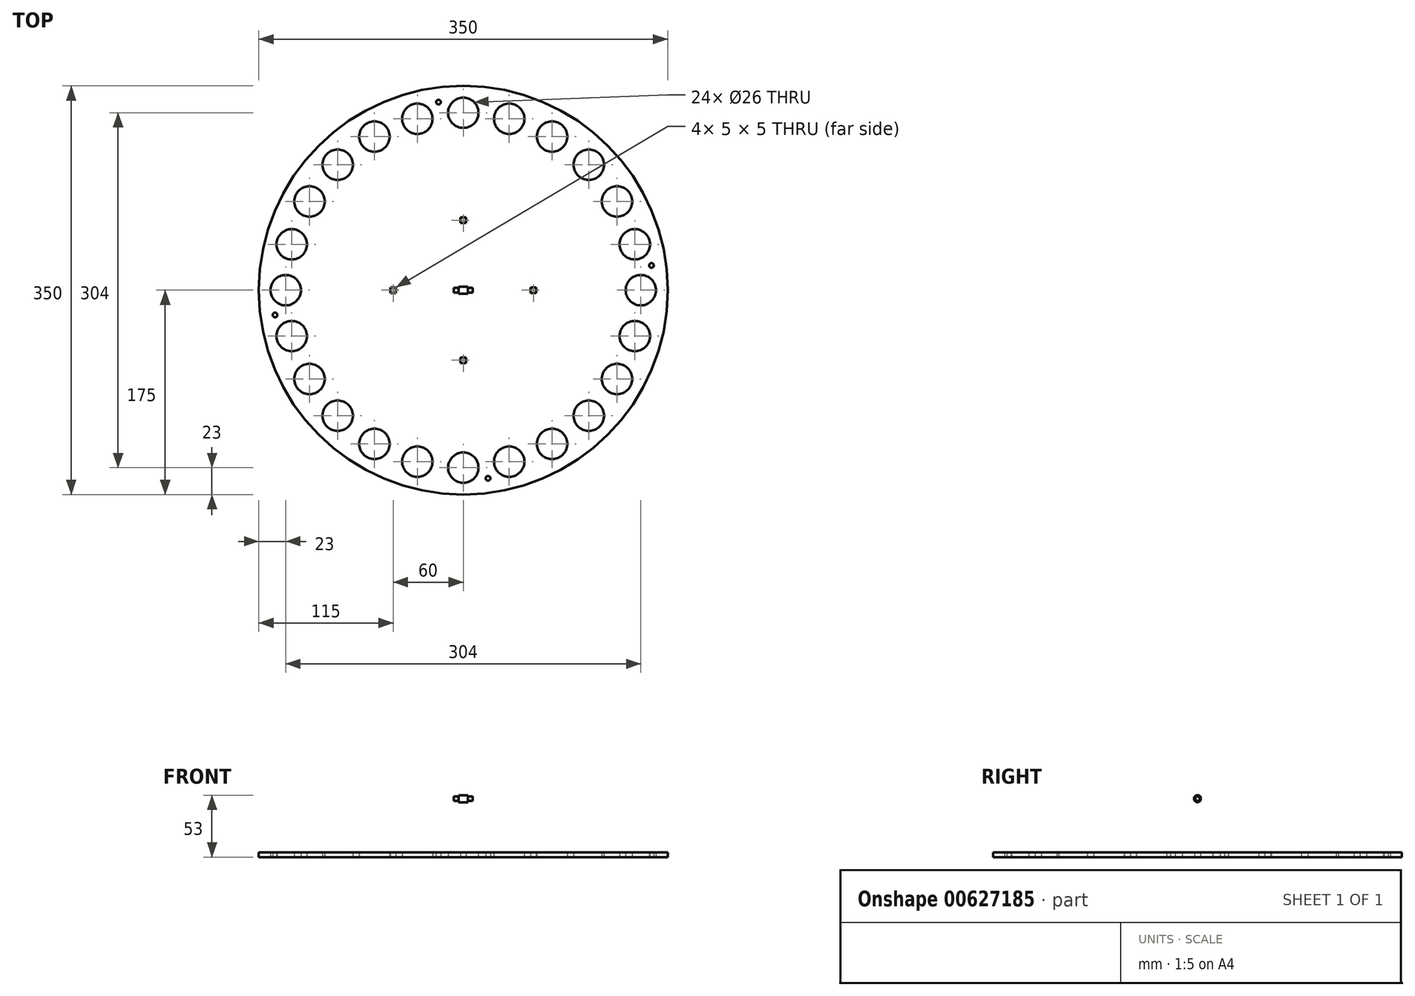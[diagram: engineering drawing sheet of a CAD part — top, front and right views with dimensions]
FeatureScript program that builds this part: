
annotation { "Feature Type Name" : "Feature", "Feature Type Description" : "" }
export const myFeature = defineFeature(function(context is Context, id is Id, definition is map)
    precondition{}
    {
        {
            var Q0;
            Q0=qCreatedBy(makeId("Top.planeOp"),FACE);
            var sketch = newSketch(context, id + "F0", { "sketchPlane" : qUnion([Q0])});
            skCircle(sketch, "E0", {"center": v(0, 0) * mm, "radius": 175 * mm});
            skLineSegment(sketch, "E1", {"start": v(0, 210.07) * mm, "end": v(0, -239.93) * mm, "construction": true});
            skLineSegment(sketch, "E2", {"start": v(-226.4, 0) * mm, "end": v(223.6, 0) * mm, "construction": true});
            skCircle(sketch, "E3", {"center": v(0, 152) * mm, "radius": 13 * mm});
            skCircle(sketch, "E4.1.1", {"center": v(-39.34, 146.82) * mm, "radius": 13 * mm});
            skCircle(sketch, "E4.2.1", {"center": v(-76, 131.64) * mm, "radius": 13 * mm});
            skCircle(sketch, "E4.3.1", {"center": v(-107.48, 107.48) * mm, "radius": 13 * mm});
            skCircle(sketch, "E4.4.1", {"center": v(-131.64, 76) * mm, "radius": 13 * mm});
            skCircle(sketch, "E4.5.1", {"center": v(-146.82, 39.34) * mm, "radius": 13 * mm});
            skCircle(sketch, "E4.6.1", {"center": v(-152, 0) * mm, "radius": 13 * mm});
            skCircle(sketch, "E4.7.1", {"center": v(-146.82, -39.34) * mm, "radius": 13 * mm});
            skCircle(sketch, "E4.8.1", {"center": v(-131.64, -76) * mm, "radius": 13 * mm});
            skCircle(sketch, "E4.9.1", {"center": v(-107.48, -107.48) * mm, "radius": 13 * mm});
            skCircle(sketch, "E4.10.1", {"center": v(-76, -131.64) * mm, "radius": 13 * mm});
            skCircle(sketch, "E4.11.1", {"center": v(-39.34, -146.82) * mm, "radius": 13 * mm});
            skCircle(sketch, "E4.12.1", {"center": v(0, -152) * mm, "radius": 13 * mm});
            skCircle(sketch, "E4.13.1", {"center": v(39.34, -146.82) * mm, "radius": 13 * mm});
            skCircle(sketch, "E4.14.1", {"center": v(76, -131.64) * mm, "radius": 13 * mm});
            skCircle(sketch, "E4.15.1", {"center": v(107.48, -107.48) * mm, "radius": 13 * mm});
            skCircle(sketch, "E4.16.1", {"center": v(131.64, -76) * mm, "radius": 13 * mm});
            skCircle(sketch, "E4.17.1", {"center": v(146.82, -39.34) * mm, "radius": 13 * mm});
            skCircle(sketch, "E4.18.1", {"center": v(152, 0) * mm, "radius": 13 * mm});
            skCircle(sketch, "E4.19.1", {"center": v(146.82, 39.34) * mm, "radius": 13 * mm});
            skCircle(sketch, "E4.20.1", {"center": v(131.64, 76) * mm, "radius": 13 * mm});
            skCircle(sketch, "E4.21.1", {"center": v(107.48, 107.48) * mm, "radius": 13 * mm});
            skCircle(sketch, "E4.22.1", {"center": v(76, 131.64) * mm, "radius": 13 * mm});
            skCircle(sketch, "E4.23.1", {"center": v(39.34, 146.82) * mm, "radius": 13 * mm});
            skLineSegment(sketch, "E5", {"start": v(0, 0) * mm, "end": v(223.08, 29.37) * mm, "construction": true});
            skCircle(sketch, "E6", {"center": v(161.1, 21.21) * mm, "radius": 2 * mm});
            skLineSegment(sketch, "E7", {"start": v(0, 0) * mm, "end": v(-29.37, 223.08) * mm, "construction": true});
            skLineSegment(sketch, "E8", {"start": v(0, 0) * mm, "end": v(-223.08, -29.37) * mm, "construction": true});
            skLineSegment(sketch, "E9", {"start": v(0, 0) * mm, "end": v(29.37, -223.08) * mm, "construction": true});
            skCircle(sketch, "E10", {"center": v(-21.21, 161.1) * mm, "radius": 2 * mm});
            skCircle(sketch, "E11", {"center": v(-161.1, -21.21) * mm, "radius": 2 * mm});
            skCircle(sketch, "E12", {"center": v(21.21, -161.1) * mm, "radius": 2 * mm});
            skLineSegment(sketch, "E13.bottom", {"start": v(2.5, 57.5) * mm, "end": v(-2.5, 57.5) * mm});
            skLineSegment(sketch, "E13.top", {"start": v(2.5, 62.5) * mm, "end": v(-2.5, 62.5) * mm});
            skLineSegment(sketch, "E13.left", {"start": v(2.5, 57.5) * mm, "end": v(2.5, 62.5) * mm});
            skLineSegment(sketch, "E13.right", {"start": v(-2.5, 57.5) * mm, "end": v(-2.5, 62.5) * mm});
            skPoint(sketch, "E13.middle", {"position": v(0, 60) * mm});
            skLineSegment(sketch, "E14.bottom", {"start": v(62.5, -2.5) * mm, "end": v(57.5, -2.5) * mm});
            skLineSegment(sketch, "E14.top", {"start": v(62.5, 2.5) * mm, "end": v(57.5, 2.5) * mm});
            skLineSegment(sketch, "E14.left", {"start": v(62.5, -2.5) * mm, "end": v(62.5, 2.5) * mm});
            skLineSegment(sketch, "E14.right", {"start": v(57.5, -2.5) * mm, "end": v(57.5, 2.5) * mm});
            skPoint(sketch, "E14.middle", {"position": v(60, 0) * mm});
            skLineSegment(sketch, "E15.bottom", {"start": v(-57.5, 2.5) * mm, "end": v(-62.5, 2.5) * mm});
            skLineSegment(sketch, "E15.top", {"start": v(-57.5, -2.5) * mm, "end": v(-62.5, -2.5) * mm});
            skLineSegment(sketch, "E15.left", {"start": v(-57.5, 2.5) * mm, "end": v(-57.5, -2.5) * mm});
            skLineSegment(sketch, "E15.right", {"start": v(-62.5, 2.5) * mm, "end": v(-62.5, -2.5) * mm});
            skPoint(sketch, "E15.middle", {"position": v(-60, 0) * mm});
            skLineSegment(sketch, "E16.bottom", {"start": v(-2.5, -57.5) * mm, "end": v(2.5, -57.5) * mm});
            skLineSegment(sketch, "E16.top", {"start": v(-2.5, -62.5) * mm, "end": v(2.5, -62.5) * mm});
            skLineSegment(sketch, "E16.left", {"start": v(-2.5, -57.5) * mm, "end": v(-2.5, -62.5) * mm});
            skLineSegment(sketch, "E16.right", {"start": v(2.5, -57.5) * mm, "end": v(2.5, -62.5) * mm});
            skPoint(sketch, "E16.middle", {"position": v(0, -60) * mm});
            skSolve(sketch);
        }
        {
            var Q0;
            Q0=makeQuery(id+"F0.imprint","IMPRINT",FACE,{"disambiguationData":[TD([[makeQuery(id+"F0.imprint","IMPRINT",EDGE,{"derivedFrom":sQuery(id+"F0.wireOp",EDGE,"E3")}),-1.0]])]});
            extrude(context, id + "F1", {"entities" : qUnion([Q0]), "depth" : 4 * mm, "offsetDistance" : 25 * mm});
        }
        {
            var Q0;
            Q0=qCreatedBy(makeId("Right.planeOp"),FACE);
            var sketch = newSketch(context, id + "F2", { "sketchPlane" : qUnion([Q0])});
            skLineSegment(sketch, "E17", {"start": v(0, 0) * mm, "end": v(0, 85) * mm, "construction": true});
            skCircle(sketch, "E18", {"center": v(0, 50) * mm, "radius": 3 * mm});
            skCircle(sketch, "E19", {"center": v(0, 50) * mm, "radius": 2 * mm});
            skSolve(sketch);
        }
        {
            var Q0;
            Q0=makeQuery(id+"F2.imprint","IMPRINT",FACE,{"disambiguationData":[TD([[makeQuery(id+"F2.imprint","IMPRINT",EDGE,{"derivedFrom":sQuery(id+"F2.wireOp",EDGE,"E18")}),1.0]])]});
            extrude(context, id + "F3", {"entities" : qUnion([Q0]), "depth" : 8 * mm, "offsetDistance" : 25 * mm, "symmetric" : true});
        }
        {
            var Q0;
            Q0=makeQuery(id+"F2.imprint","IMPRINT",FACE,{"disambiguationData":[TD([[makeQuery(id+"F2.imprint","IMPRINT",EDGE,{"derivedFrom":sQuery(id+"F2.wireOp",EDGE,"E19")}),1.0]])]});
            extrude(context, id + "F4", {"entities" : qUnion([Q0]), "operationType" : NewBodyOperationType.ADD, "depth" : 16 * mm, "offsetDistance" : 25 * mm, "symmetric" : true});
        }
    });
